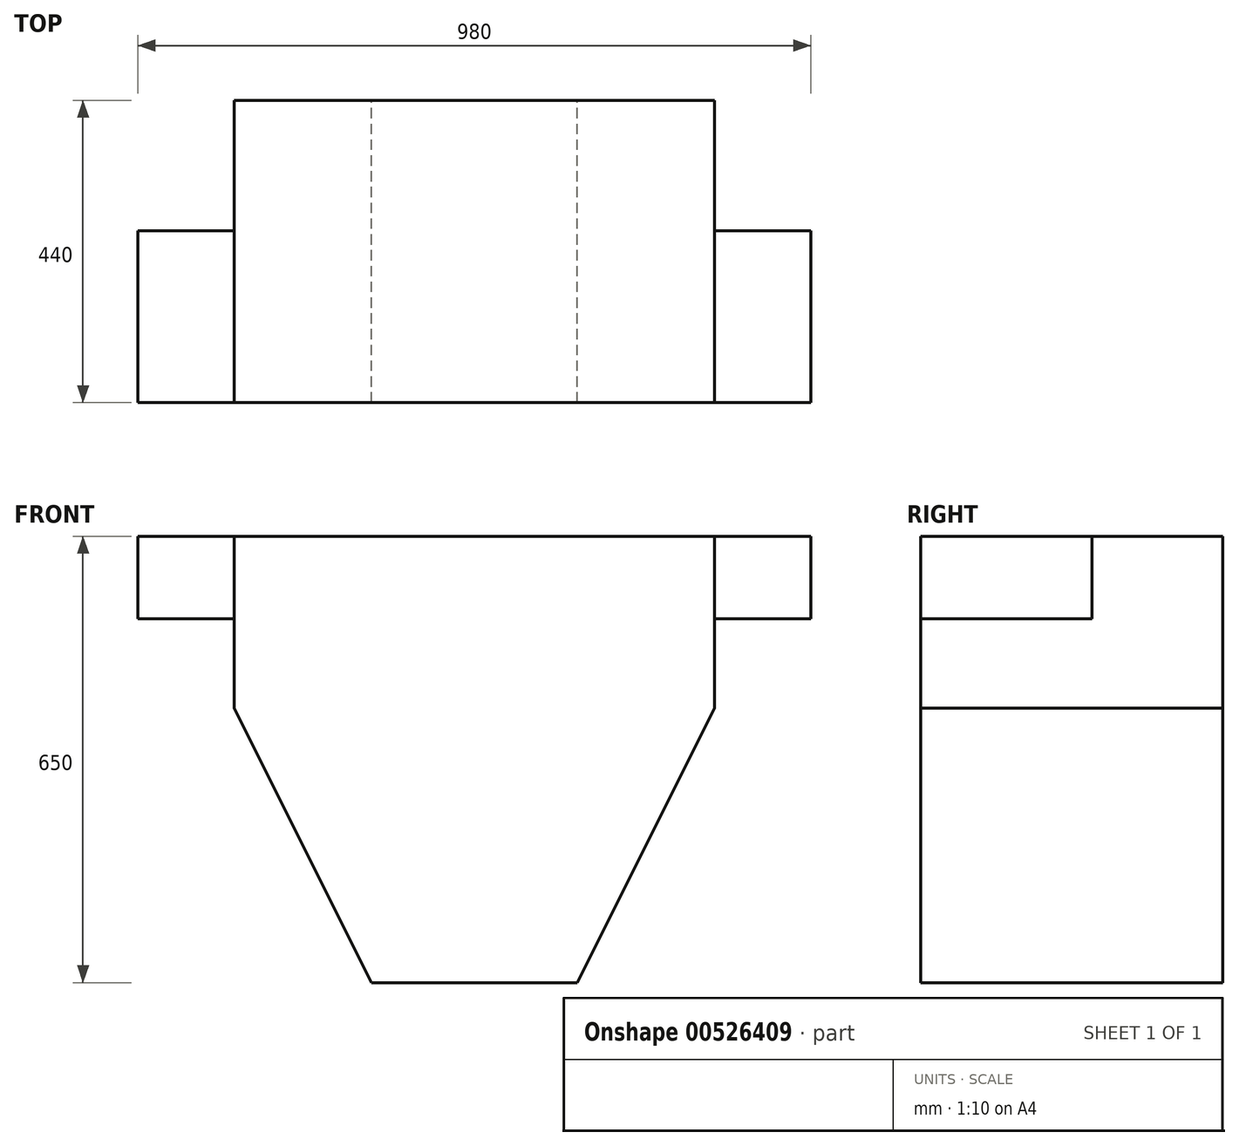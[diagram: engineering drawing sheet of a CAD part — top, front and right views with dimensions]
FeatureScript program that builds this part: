
annotation { "Feature Type Name" : "Feature", "Feature Type Description" : "" }
export const myFeature = defineFeature(function(context is Context, id is Id, definition is map)
    precondition{}
    {
        {
            var Q0;
            Q0=qCreatedBy(makeId("Front.planeOp"),FACE);
            var sketch = newSketch(context, id + "F0", { "sketchPlane" : qUnion([Q0])});
            skLineSegment(sketch, "E0.bottom", {"start": v(150, -325) * mm, "end": v(-150, -325) * mm});
            skLineSegment(sketch, "E0.top", {"start": v(350, 325) * mm, "end": v(-350, 325) * mm});
            skLineSegment(sketch, "E0.left", {"start": v(350, 75) * mm, "end": v(350, 325) * mm});
            skLineSegment(sketch, "E0.right", {"start": v(-350, 75) * mm, "end": v(-350, 325) * mm});
            skPoint(sketch, "E0.middle", {"position": v(0, 0) * mm});
            skLineSegment(sketch, "E1", {"start": v(350, 75) * mm, "end": v(150, -325) * mm});
            skLineSegment(sketch, "E2", {"start": v(-350, 75) * mm, "end": v(-150, -325) * mm});
            skSolve(sketch);
        }
        {
            var Q0;
            Q0 = qSketchRegion(id + "F0", true);
            extrude(context, id + "F1", {"entities" : qUnion([Q0]), "depth" : 440 * mm, "offsetDistance" : 25 * mm});
        }
        {
            var Q0;
            Q0=makeQuery(id+"F1.opExtrude","CAP_FACE",FACE,{"disambiguationData":[OSD([sQuery(id+"F0.wireOp",EDGE,"E0.bottom"),sQuery(id+"F0.wireOp",EDGE,"E0.top"),sQuery(id+"F0.wireOp",EDGE,"E0.left"),sQuery(id+"F0.wireOp",EDGE,"E0.right"),sQuery(id+"F0.wireOp",EDGE,"E1"),sQuery(id+"F0.wireOp",EDGE,"E2")])],"isStart":false});
            var sketch = newSketch(context, id + "F2", { "sketchPlane" : qUnion([Q0])});
            skLineSegment(sketch, "E3", {"start": v(-350, 325) * mm, "end": v(-490, 325) * mm});
            skLineSegment(sketch, "E4", {"start": v(-490, 325) * mm, "end": v(-490, 205) * mm});
            skLineSegment(sketch, "E5", {"start": v(-490, 205) * mm, "end": v(-350, 205) * mm});
            skLineSegment(sketch, "E6", {"start": v(-350, 205) * mm, "end": v(-350, 325) * mm});
            skLineSegment(sketch, "E7", {"start": v(350, 325) * mm, "end": v(490, 325) * mm});
            skLineSegment(sketch, "E8", {"start": v(490, 325) * mm, "end": v(490, 205) * mm});
            skLineSegment(sketch, "E9", {"start": v(490, 205) * mm, "end": v(350, 205) * mm});
            skLineSegment(sketch, "E10", {"start": v(350, 205) * mm, "end": v(350, 325) * mm});
            skSolve(sketch);
        }
        {
            var Q0;
            Q0=makeQuery(id+"F2.imprint","IMPRINT",FACE,{"disambiguationData":[TD([[makeQuery(id+"F2.imprint","IMPRINT",EDGE,{"derivedFrom":sQuery(id+"F2.wireOp",EDGE,"E7")}),-1.0]])]});
            var Q1;
            Q1=makeQuery(id+"F2.imprint","IMPRINT",FACE,{"disambiguationData":[TD([[makeQuery(id+"F2.imprint","IMPRINT",EDGE,{"derivedFrom":sQuery(id+"F2.wireOp",EDGE,"E3")}),1.0]])]});
            extrude(context, id + "F3", {"entities" : qUnion([Q0, Q1]), "oppositeDirection" : true, "depth" : 250 * mm, "offsetDistance" : 25 * mm});
        }
    });
